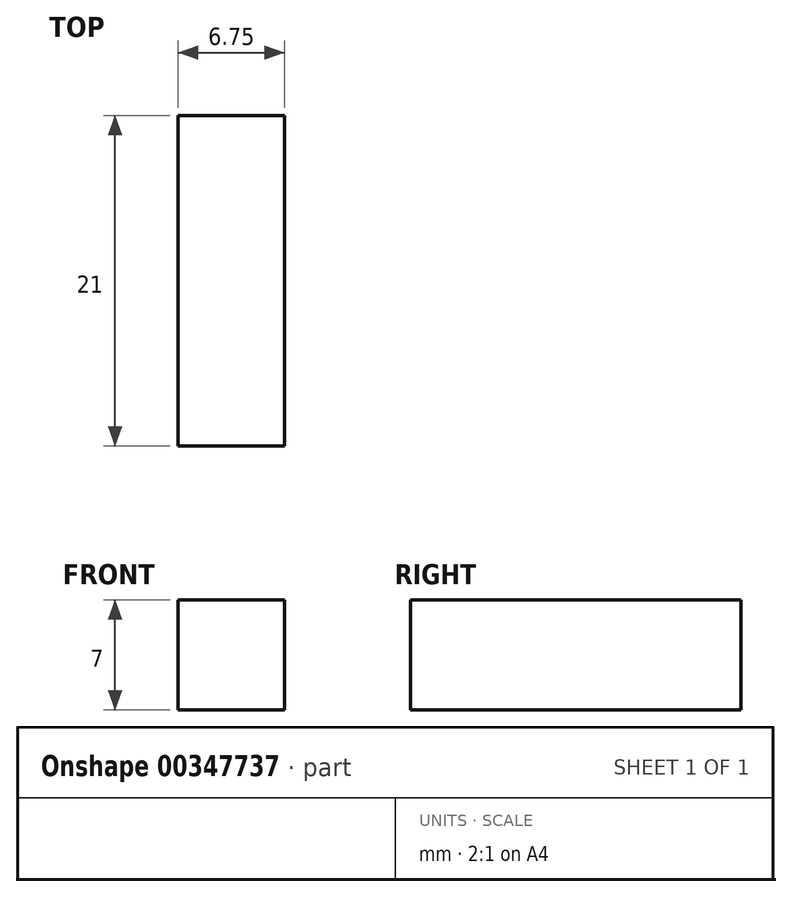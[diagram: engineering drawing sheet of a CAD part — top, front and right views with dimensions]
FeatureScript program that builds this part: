
annotation { "Feature Type Name" : "Feature", "Feature Type Description" : "" }
export const myFeature = defineFeature(function(context is Context, id is Id, definition is map)
    precondition{}
    {
        {
            var Q0;
            Q0=qCreatedBy(makeId("Top.planeOp"),FACE);
            var sketch = newSketch(context, id + "F0", { "sketchPlane" : qUnion([Q0])});
            skLineSegment(sketch, "E0.bottom", {"start": v(1.7, 7.36) * mm, "end": v(8.46, 7.36) * mm});
            skLineSegment(sketch, "E0.top", {"start": v(1.7, -13.64) * mm, "end": v(8.46, -13.64) * mm});
            skLineSegment(sketch, "E0.left", {"start": v(1.7, 7.36) * mm, "end": v(1.7, -13.64) * mm});
            skLineSegment(sketch, "E0.right", {"start": v(8.46, 7.36) * mm, "end": v(8.46, -13.64) * mm});
            skSolve(sketch);
        }
        {
            var Q0;
            Q0 = qSketchRegion(id + "F0", true);
            extrude(context, id + "F1", {"entities" : qUnion([Q0]), "depth" : 7 * mm});
        }
    });
